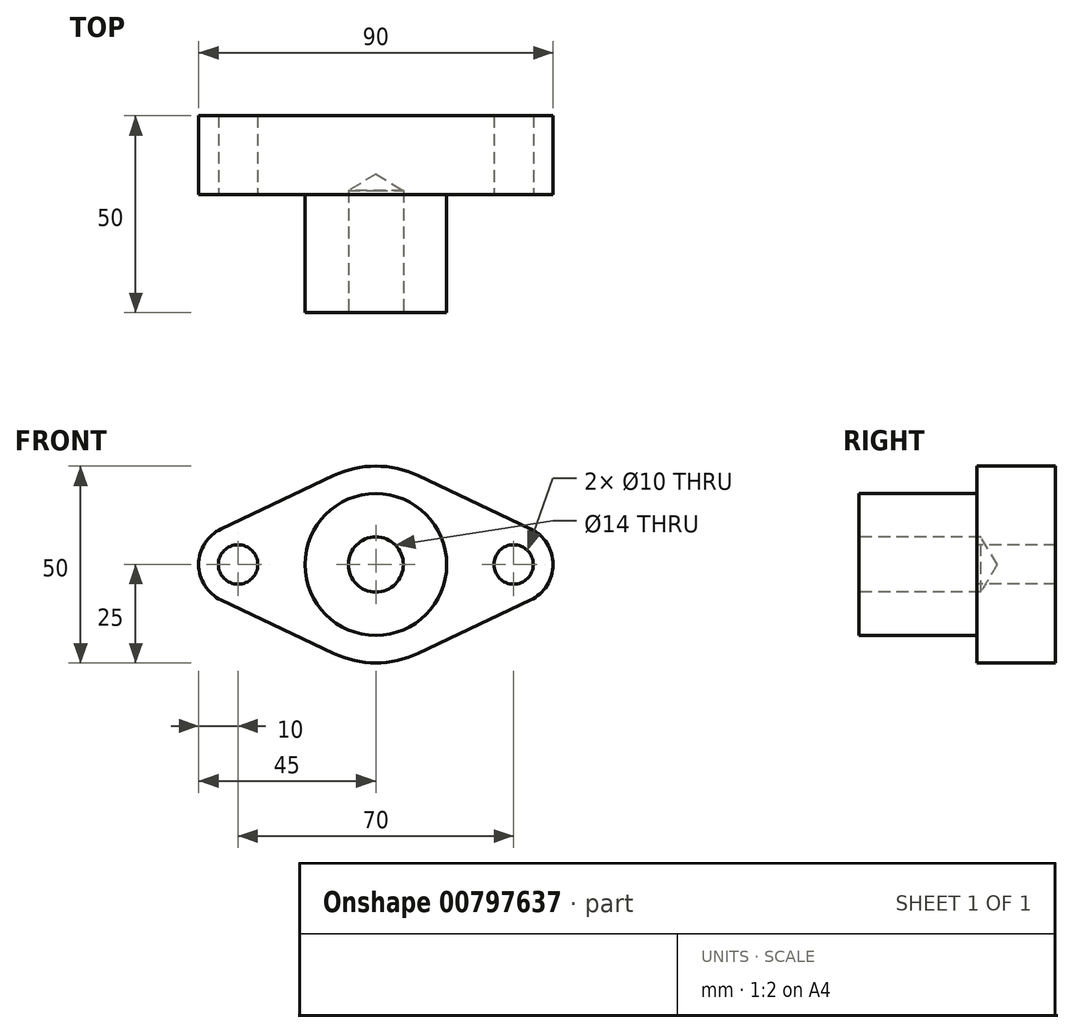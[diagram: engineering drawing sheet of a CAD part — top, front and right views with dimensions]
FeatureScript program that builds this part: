
annotation { "Feature Type Name" : "Feature", "Feature Type Description" : "" }
export const myFeature = defineFeature(function(context is Context, id is Id, definition is map)
    precondition{}
    {
        {
            var Q0;
            Q0=qCreatedBy(makeId("Front.planeOp"),FACE);
            var sketch = newSketch(context, id + "F0", { "sketchPlane" : qUnion([Q0])});
            skArc(sketch, "E0", {"start": v(10.71, 22.59) * mm, "mid": v(0, 25) * mm, "end": v(-10.71, 22.59) * mm});
            skArc(sketch, "E1", {"start": v(-39.29, 9.04) * mm, "mid": v(-45, 0) * mm, "end": v(-39.29, -9.04) * mm});
            skArc(sketch, "E2", {"start": v(39.29, -9.04) * mm, "mid": v(45, 0) * mm, "end": v(39.29, 9.04) * mm});
            skLineSegment(sketch, "E3", {"start": v(-39.29, 9.04) * mm, "end": v(-10.71, 22.59) * mm});
            skLineSegment(sketch, "E4", {"start": v(10.71, 22.59) * mm, "end": v(39.29, 9.04) * mm});
            skLineSegment(sketch, "E5", {"start": v(-39.29, -9.04) * mm, "end": v(-10.71, -22.59) * mm});
            skLineSegment(sketch, "E6", {"start": v(10.71, -22.59) * mm, "end": v(39.29, -9.04) * mm});
            skArc(sketch, "E7.trimOffspring", {"start": v(-10.71, -22.59) * mm, "mid": v(0, -25) * mm, "end": v(10.71, -22.59) * mm});
            skSolve(sketch);
        }
        {
            var Q0;
            Q0=makeQuery(id+"F0.imprint","IMPRINT",FACE,{"disambiguationData":[TD([[makeQuery(id+"F0.imprint","IMPRINT",EDGE,{"derivedFrom":sQuery(id+"F0.wireOp",EDGE,"E0")}),1.0]])]});
            extrude(context, id + "F1", {"entities" : qUnion([Q0]), "depth" : 20 * mm, "offsetDistance" : 25 * mm});
        }
        {
            var Q0;
            Q0=makeQuery(id+"F1.opExtrude","CAP_FACE",FACE,{"disambiguationData":[OSD([sQuery(id+"F0.wireOp",EDGE,"E0"),sQuery(id+"F0.wireOp",EDGE,"E1"),sQuery(id+"F0.wireOp",EDGE,"E2"),sQuery(id+"F0.wireOp",EDGE,"E3"),sQuery(id+"F0.wireOp",EDGE,"E4"),sQuery(id+"F0.wireOp",EDGE,"E5"),sQuery(id+"F0.wireOp",EDGE,"E6"),sQuery(id+"F0.wireOp",EDGE,"E7.trimOffspring")])],"isStart":false});
            var sketch = newSketch(context, id + "F2", { "sketchPlane" : qUnion([Q0])});
            skCircle(sketch, "E8", {"center": v(0, 0) * mm, "radius": 18 * mm});
            skSolve(sketch);
        }
        {
            var Q0;
            Q0=makeQuery(id+"F2.imprint","IMPRINT",FACE,{"disambiguationData":[TD([[makeQuery(id+"F2.imprint","IMPRINT",EDGE,{"derivedFrom":sQuery(id+"F2.wireOp",EDGE,"E8")}),1.0]])]});
            extrude(context, id + "F3", {"entities" : qUnion([Q0]), "operationType" : NewBodyOperationType.ADD, "depth" : 30 * mm, "offsetDistance" : 25 * mm});
        }
        {
            var Q0;
            Q0=makeQuery(id+"F3.opExtrude","CAP_FACE",FACE,{"disambiguationData":[OSD([sQuery(id+"F2.wireOp",EDGE,"E8")])],"isStart":false});
            var sketch = newSketch(context, id + "F4", { "sketchPlane" : qUnion([Q0])});
            skPoint(sketch, "E9", {"position": v(0, 0) * mm});
            skSolve(sketch);
        }
        {
            var Q0;
            Q0=makeQuery(id+"F1.opExtrude","CAP_FACE",FACE,{"disambiguationData":[OSD([sQuery(id+"F0.wireOp",EDGE,"E0"),sQuery(id+"F0.wireOp",EDGE,"E1"),sQuery(id+"F0.wireOp",EDGE,"E2"),sQuery(id+"F0.wireOp",EDGE,"E3"),sQuery(id+"F0.wireOp",EDGE,"E4"),sQuery(id+"F0.wireOp",EDGE,"E5"),sQuery(id+"F0.wireOp",EDGE,"E6"),sQuery(id+"F0.wireOp",EDGE,"E7.trimOffspring")])],"isStart":false});
            var sketch = newSketch(context, id + "F5", { "sketchPlane" : qUnion([Q0])});
            skPoint(sketch, "E10", {"position": v(-35, 0) * mm});
            skPoint(sketch, "E11", {"position": v(35, 0) * mm});
            skSolve(sketch);
        }
        {
            var Q0;
            Q0=sQuery(id+"F5.wireOp",VERTEX,"E11");
            var Q1;
            Q1=sQuery(id+"F5.wireOp",VERTEX,"E10");
            var Q2;
            Q2=makeQuery(id+"F1.opExtrude","SWEPT_BODY",BODY,{"disambiguationData":[OSD([sQuery(id+"F0.wireOp",EDGE,"E0"),sQuery(id+"F0.wireOp",EDGE,"E1"),sQuery(id+"F0.wireOp",EDGE,"E2"),sQuery(id+"F0.wireOp",EDGE,"E3"),sQuery(id+"F0.wireOp",EDGE,"E4"),sQuery(id+"F0.wireOp",EDGE,"E5"),sQuery(id+"F0.wireOp",EDGE,"E6"),sQuery(id+"F0.wireOp",EDGE,"E7.trimOffspring")])]});
            hole(context, id + "F6", {"style" : HoleStyle.SIMPLE, "endStyle" : HoleEndStyle.THROUGH, "holeDiameter" : 10 * mm, "majorDiameter" : 5 * mm, "isTappedThrough" : true, "tappedDepth" : 12 * mm, "tapClearance" : 3, "locations" : qUnion([Q0, Q1]), "scope" : qUnion([Q2])});
        }
        {
            var Q0;
            Q0=sQuery(id+"F4.wireOp",VERTEX,"E9");
            var Q1;
            Q1=makeQuery(id+"F1.opExtrude","SWEPT_BODY",BODY,{"disambiguationData":[OSD([sQuery(id+"F0.wireOp",EDGE,"E0"),sQuery(id+"F0.wireOp",EDGE,"E1"),sQuery(id+"F0.wireOp",EDGE,"E2"),sQuery(id+"F0.wireOp",EDGE,"E3"),sQuery(id+"F0.wireOp",EDGE,"E4"),sQuery(id+"F0.wireOp",EDGE,"E5"),sQuery(id+"F0.wireOp",EDGE,"E6"),sQuery(id+"F0.wireOp",EDGE,"E7.trimOffspring")])]});
            hole(context, id + "F7", {"style" : HoleStyle.SIMPLE, "endStyle" : HoleEndStyle.BLIND, "standardTappedOrClearance" : lookupTablePath({ "standard" : "ISO", "engagement" : "75%", "pitch" : "2 mm", "size" : "M16", "type" : "Tapped" }), "standardBlindInLast" : lookupTablePath({ "standard" : "ISO", "engagement" : "75%", "pitch" : "2 mm", "size" : "M16", "type" : "Tapped" }), "holeDiameter" : 14 * mm, "majorDiameter" : 16 * mm, "showTappedDepth" : true, "holeDepth" : 31 * mm, "isTappedThrough" : true, "tappedDepth" : 25 * mm, "tapClearance" : 3, "locations" : qUnion([Q0]), "scope" : qUnion([Q1])});
        }
    });
